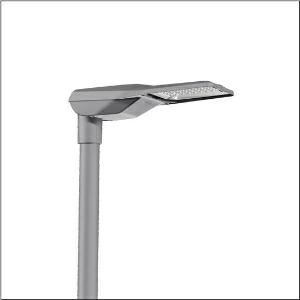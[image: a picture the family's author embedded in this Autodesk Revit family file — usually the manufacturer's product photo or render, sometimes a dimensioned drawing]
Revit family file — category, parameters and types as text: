
# Revit family: streetlight_sl_21_iq_mini___st1_5a_5xe2p41d08hb_72ee
name_source: partatom
category: Lighting Fixtures
units: mm (PartAtom-declared; Revit-internal decimal feet)

## family parameters
Cut with Voids When Loaded = No
Host = Face
Light Source = No
Part Type = Normal
Room Calculation Point = No
Round Connector Dimension = Use Diameter
Shared = No

## types (1)
- --- (1 x LED, 9690 lm, 70.9 W, 4000K)
    Apparent Load = 71 VA
    CIE Flux Codes = 22 53 95 100 100
    Color Rendering = 70
    Color Temperature = 4000K
    Default Elevation = 1800 mm
    Description = Streetlight SL 21 iQ mini, mast luminaire, primary light control with lens, of PMMA, primary optical cover: cover, of toughened safety glass, transparent, light distribution: ST1.5a, light emission: direct distribution, primary light characteristic: asymmetric, installation type: post-top, side-entry, LED, High Power LED, rated luminous flux: 9.690lm, luminous efficacy: 137lm/W, light colour: 740, colour temperature: 4000K, control: Auto-Match, Temp-Guard, Lumen-Switch, Night-Set, Smart-Wire, Light-Fading, Desk-Remote (wireless, voltage-free reading and setting of iQ features in the workshop via application-optimized NFC function/RFID function), optimised constant luminous flux control (CLO 2.0), pre-setting: linear dimming characteristic, mains connection: 220..240V, AC, 50/60Hz, start of lifetime: 71W, end of service life: 75W, reduction: 31W, luminaire housing, of diecast aluminium, powder-coated, Siteco® metallic grey (DB 702S), corrosivity category C5 mid according to DIN EN ISO 12944, please order mast flange separately, inclination adjustable: 0°, 5°, 10°, 15°, sealing non-destructively replaceable, multi-level sealing system, length: 628mm, width: 235mm, height: 110mm, mast flange for spigot size: 42mm (side-entry): 5XC10008XM4, 60/48mm (side-entry/post-top): 5XC10108XM2, 76/60mm (side-entry/post-top): 5XC10108XM1, protection rating (complete): IP66, insulation class (complete): insulation class II (safety insulation), certification: CE, ENEC, ENEC+, VDE, impact resistance: IK09, permissible operating ambient temperature for outdoor applications: -40..+50°C, standard-compliant lighting for roads and squares, packaging unit: 1 piece

Light Distribution: ST1.5a
    Height = 110 mm
    Lamp = 1 x LED
    Lamp Light Flux = 9690 lm
    Lamp Power = 70.9 W
    Lamp count = 1
    Length = 625 mm
    Luminous efficacy = 137 lm/W
    Manufacturer = Siteco
    ModVariant = No
    Model = 5XE2P41D08HB
    Number of Poles = 1
    OnlyDefault = Yes
    Power Factor = 1
    Product Name = Streetlight SL 21 iQ mini | ST1.5a
    Product group = mast luminaire | pylon top
    ProductGroupID = 6100
    Protection Class = Protection class II
    Protection Degree = IP 66
    RLX_Detail_Level = 1
    RLX_Emergency_Light_Flux = 0 lm
    RLX_Emergency_Type = 0
    RLX_Emergency_Type_DB = No
    RlxData = <blob elided: 95905 chars, md5=101701c1>
    Socket = socket
    Standby Power = 0 W
    System Light Flux = 9690 lm
    System Power = 71 W
    Type Comments = factory setting: luminous flux: 100 % | dim-lin: 254 | 711 mA
    Type Image = l_1003519.jpg
    URL = http://relux.com
    VarID = @adj_127381
    Voltage = 0 V
    Weight = 0.00 kg
    Width = 234 mm

## geometry (parser evidence)
native form markers: Blend x4, Sweep x11
no freeform markers — native parametric forms only
